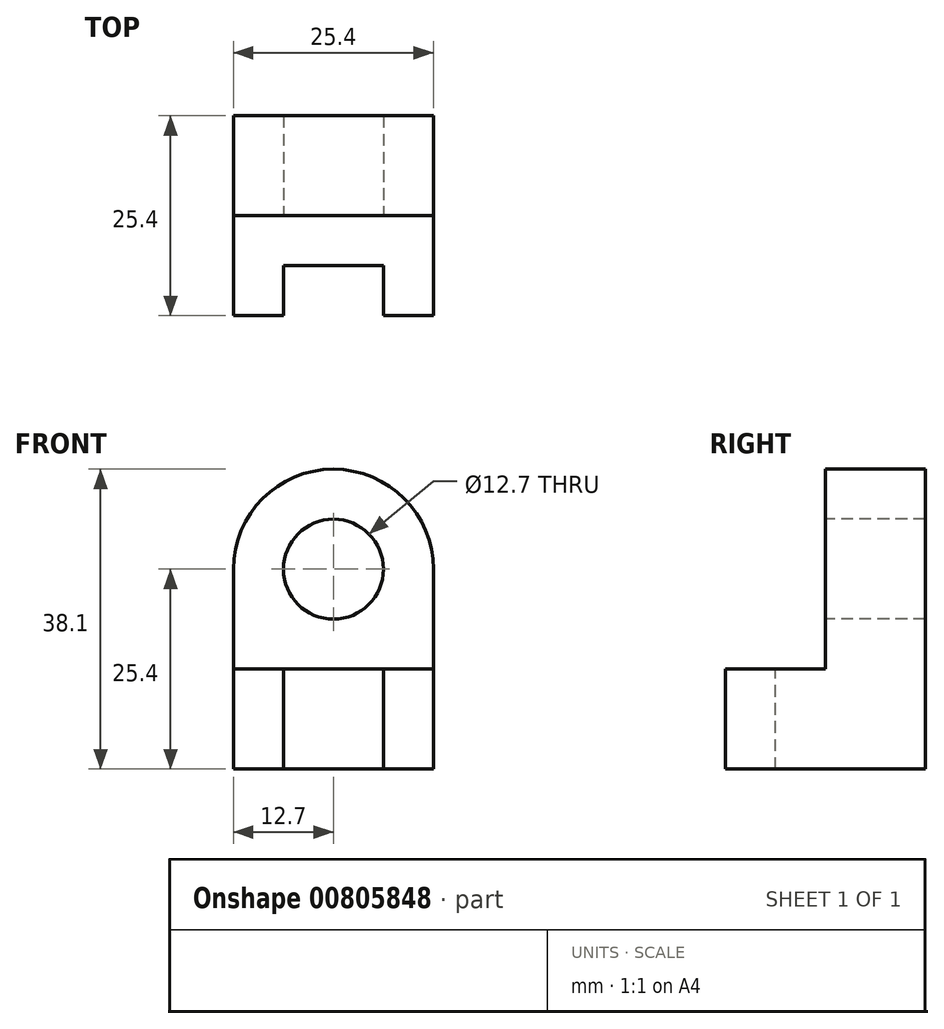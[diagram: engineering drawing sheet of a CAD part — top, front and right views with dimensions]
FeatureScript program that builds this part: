
annotation { "Feature Type Name" : "Feature", "Feature Type Description" : "" }
export const myFeature = defineFeature(function(context is Context, id is Id, definition is map)
    precondition{}
    {
        {
            var Q0;
            Q0=qCreatedBy(makeId("Right.planeOp"),FACE);
            var sketch = newSketch(context, id + "F0", { "sketchPlane" : qUnion([Q0])});
            skLineSegment(sketch, "E0", {"start": v(0, 0) * mm, "end": v(-25.4, 0) * mm});
            skLineSegment(sketch, "E1", {"start": v(-25.4, 0) * mm, "end": v(-25.4, 12.7) * mm});
            skLineSegment(sketch, "E2", {"start": v(-25.4, 12.7) * mm, "end": v(-12.7, 12.7) * mm});
            skLineSegment(sketch, "E3", {"start": v(-12.7, 12.7) * mm, "end": v(-12.7, 57.15) * mm});
            skLineSegment(sketch, "E4", {"start": v(-12.7, 57.15) * mm, "end": v(0, 57.15) * mm});
            skLineSegment(sketch, "E5", {"start": v(0, 57.15) * mm, "end": v(0, 0) * mm});
            skSolve(sketch);
        }
        {
            var Q0;
            Q0=makeQuery(id+"F0.imprint","IMPRINT",FACE,{"disambiguationData":[TD([[makeQuery(id+"F0.imprint","IMPRINT",EDGE,{"derivedFrom":sQuery(id+"F0.wireOp",EDGE,"E0")}),-1.0]])]});
            extrude(context, id + "F1", {"entities" : qUnion([Q0]), "depth" : 25.4 * mm, "offsetDistance" : 25.4 * mm});
        }
        {
            var Q0;
            Q0=makeQuery(id+"F1.opExtrude","SWEPT_FACE",FACE,{"disambiguationData":[OSD([sQuery(id+"F0.wireOp",EDGE,"E1")])]});
            var sketch = newSketch(context, id + "F2", { "sketchPlane" : qUnion([Q0])});
            skLineSegment(sketch, "E6", {"start": v(0, 0) * mm, "end": v(6.35, 0) * mm});
            skLineSegment(sketch, "E7", {"start": v(6.35, 0) * mm, "end": v(6.35, 12.7) * mm});
            skLineSegment(sketch, "E8", {"start": v(6.35, 12.7) * mm, "end": v(19.05, 12.7) * mm});
            skLineSegment(sketch, "E9", {"start": v(19.05, 12.7) * mm, "end": v(19.05, 0) * mm});
            skSolve(sketch);
        }
        {
            var Q0;
            {var subQ0=sQuery(id+"F2.wireOp",EDGE,"E7");Q0=makeQuery(id+"F2.imprint","IMPRINT",FACE,{"disambiguationData":[TD([[makeQuery(id+"F2.imprint","IMPRINT",EDGE,{"derivedFrom":subQ0}),-1.0]])]});}
            extrude(context, id + "F3", {"entities" : qUnion([Q0]), "operationType" : NewBodyOperationType.REMOVE, "oppositeDirection" : true, "depth" : 6.35 * mm, "offsetDistance" : 25.4 * mm});
        }
        {
            var Q0;
            Q0=makeQuery(id+"F1.opExtrude","SWEPT_FACE",FACE,{"disambiguationData":[OSD([sQuery(id+"F0.wireOp",EDGE,"E3")])]});
            var sketch = newSketch(context, id + "F4", { "sketchPlane" : qUnion([Q0])});
            skLineSegment(sketch, "E10", {"start": v(0, 12.7) * mm, "end": v(0, 25.4) * mm, "construction": true});
            skLineSegment(sketch, "E11", {"start": v(0, 25.4) * mm, "end": v(12.7, 25.4) * mm, "construction": true});
            skCircle(sketch, "E12", {"center": v(12.7, 25.4) * mm, "radius": 6.35 * mm});
            skSolve(sketch);
        }
        {
            var Q0;
            Q0=makeQuery(id+"F4.imprint","IMPRINT",FACE,{"disambiguationData":[TD([[makeQuery(id+"F4.imprint","IMPRINT",EDGE,{"derivedFrom":sQuery(id+"F4.wireOp",EDGE,"E12")}),1.0]])]});
            extrude(context, id + "F5", {"entities" : qUnion([Q0]), "operationType" : NewBodyOperationType.REMOVE, "oppositeDirection" : true, "depth" : 12.7 * mm, "offsetDistance" : 25.4 * mm});
        }
        {
            var Q0;
            Q0=makeQuery(id+"F1.opExtrude","SWEPT_FACE",FACE,{"disambiguationData":[OSD([sQuery(id+"F0.wireOp",EDGE,"E3")])]});
            var sketch = newSketch(context, id + "F6", { "sketchPlane" : qUnion([Q0])});
            skLineSegment(sketch, "E13", {"start": v(0, 12.7) * mm, "end": v(0, 25.4) * mm, "construction": true});
            skLineSegment(sketch, "E14", {"start": v(25.4, 12.7) * mm, "end": v(25.4, 25.4) * mm, "construction": true});
            skArc(sketch, "E15", {"start": v(25.4, 25.4) * mm, "mid": v(12.7, 38.1) * mm, "end": v(0, 25.4) * mm});
            skSolve(sketch);
        }
        {
            var Q0;
            {var subQ0=sQuery(id+"F6.wireOp",EDGE,"E15");Q0=makeQuery(id+"F6.imprint","IMPRINT",FACE,{"disambiguationData":[TD([[makeQuery(id+"F6.imprint","IMPRINT",EDGE,{"derivedFrom":subQ0}),-1.0]])]});}
            extrude(context, id + "F7", {"entities" : qUnion([Q0]), "operationType" : NewBodyOperationType.REMOVE, "oppositeDirection" : true, "depth" : 25.4 * mm, "offsetDistance" : 25.4 * mm});
        }
    });
